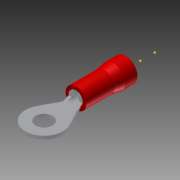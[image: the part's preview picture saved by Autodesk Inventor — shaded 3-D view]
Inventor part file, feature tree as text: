
AUTODESK INVENTOR PART (.ipt)
format: ipt  version: 2011 (Build 150239000, 239)  size: 172,032 bytes
history: native  units: mm
features: other x4, plane x2, imported_body x1, sketch x1
ambient origin geometry x8: Origin, YZ Plane, XZ Plane, XY Plane, X Axis, Y Axis, Z Axis, Center Point
bodies: Solid1 (feature_tree)
feature tree (8):
  imported_body  "Base1"
  sketch  "Sketch1"  dims[d0=3.175mm d1=6.35mm]
  other  "Work Point2"
  other  "Work Point3"
  plane  "Work Plane1"
  other  "Work Axis1"
  plane  "Work Plane2"
  other  "Work Axis2"
